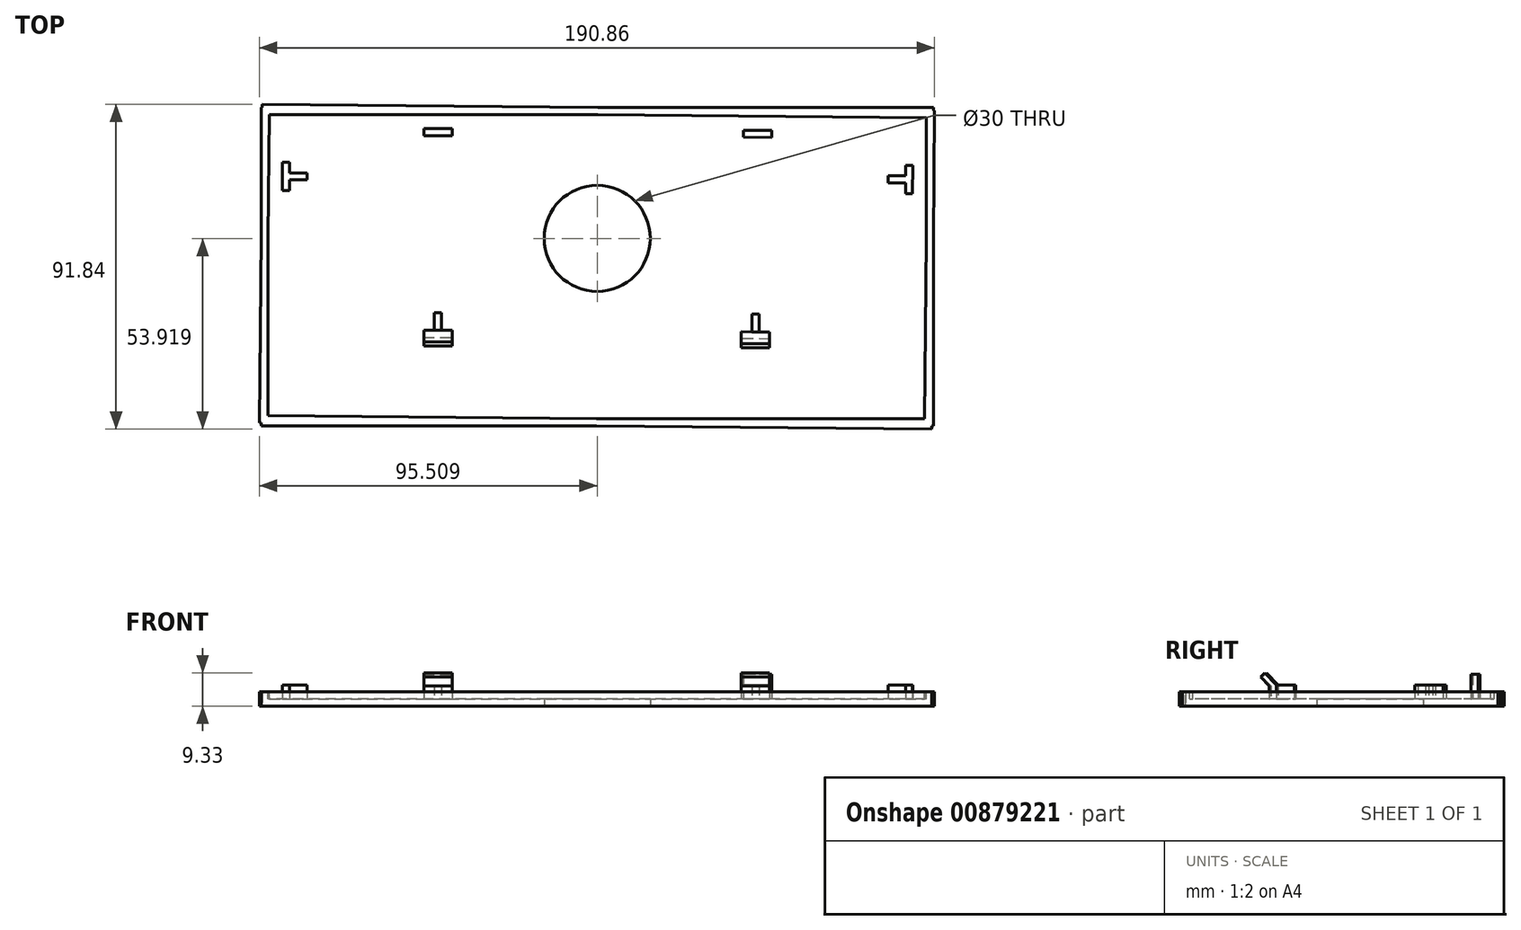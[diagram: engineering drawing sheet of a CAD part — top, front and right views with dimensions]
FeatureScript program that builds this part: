
annotation { "Feature Type Name" : "Feature", "Feature Type Description" : "" }
export const myFeature = defineFeature(function(context is Context, id is Id, definition is map)
    precondition{}
    {
        {
            var Q0;
            Q0=qCreatedBy(makeId("Top.planeOp"),FACE);
            var sketch = newSketch(context, id + "F0", { "sketchPlane" : qUnion([Q0])});
            skLineSegment(sketch, "E0.bottom", {"start": v(-112.44, 46.32) * mm, "end": v(77.56, 46.32) * mm});
            skLineSegment(sketch, "E0.top", {"start": v(-112.44, -43.68) * mm, "end": v(77.56, -43.68) * mm});
            skLineSegment(sketch, "E0.left", {"start": v(-112.44, 46.32) * mm, "end": v(-112.44, -43.68) * mm});
            skLineSegment(sketch, "E0.right", {"start": v(77.56, 46.32) * mm, "end": v(77.56, -43.68) * mm});
            skLineSegment(sketch, "E1.0", {"start": v(-110.44, 44.32) * mm, "end": v(-110.44, -41.68) * mm});
            skLineSegment(sketch, "E1.1", {"start": v(-110.44, 44.32) * mm, "end": v(75.56, 44.32) * mm});
            skLineSegment(sketch, "E1.2", {"start": v(75.56, 44.32) * mm, "end": v(75.56, -41.68) * mm});
            skLineSegment(sketch, "E1.3", {"start": v(-110.44, -41.68) * mm, "end": v(75.56, -41.68) * mm});
            skCircle(sketch, "E2", {"center": v(-17.44, 9.32) * mm, "radius": 15 * mm});
            skLineSegment(sketch, "E3.bottom", {"start": v(-106.44, 30.84) * mm, "end": v(-104.44, 30.84) * mm});
            skLineSegment(sketch, "E3.top", {"start": v(-106.44, 22.84) * mm, "end": v(-104.44, 22.84) * mm});
            skLineSegment(sketch, "E3.left", {"start": v(-106.44, 30.84) * mm, "end": v(-106.44, 22.84) * mm});
            skLineSegment(sketch, "E3.right", {"start": v(-104.44, 30.84) * mm, "end": v(-104.44, 22.84) * mm});
            skLineSegment(sketch, "E4", {"start": v(-17.23, 53.53) * mm, "end": v(-17.44, 9.32) * mm, "construction": true});
            skLineSegment(sketch, "E5", {"start": v(-17.44, 9.32) * mm, "end": v(-17.74, -52.58) * mm, "construction": true});
            skLineSegment(sketch, "E6.MirrorCS", {"start": v(71.76, 29.98) * mm, "end": v(71.69, 21.98) * mm});
            skLineSegment(sketch, "E7.MirrorCS", {"start": v(69.76, 30) * mm, "end": v(69.69, 22) * mm});
            skLineSegment(sketch, "E8.MirrorCS", {"start": v(71.69, 21.98) * mm, "end": v(69.69, 22) * mm});
            skLineSegment(sketch, "E9.MirrorCS", {"start": v(71.76, 29.98) * mm, "end": v(69.76, 30) * mm});
            skLineSegment(sketch, "E10.bottom", {"start": v(-66.44, 40.32) * mm, "end": v(-58.44, 40.32) * mm});
            skLineSegment(sketch, "E10.top", {"start": v(-66.44, 38.32) * mm, "end": v(-58.44, 38.32) * mm});
            skLineSegment(sketch, "E10.left", {"start": v(-66.44, 40.32) * mm, "end": v(-66.44, 38.32) * mm});
            skLineSegment(sketch, "E10.right", {"start": v(-58.44, 40.32) * mm, "end": v(-58.44, 38.32) * mm});
            skLineSegment(sketch, "E11.MirrorCS", {"start": v(31.86, 39.84) * mm, "end": v(23.86, 39.92) * mm});
            skLineSegment(sketch, "E12.MirrorCS", {"start": v(31.84, 37.84) * mm, "end": v(23.84, 37.92) * mm});
            skLineSegment(sketch, "E13.MirrorCS", {"start": v(23.86, 39.92) * mm, "end": v(23.84, 37.92) * mm});
            skLineSegment(sketch, "E14.MirrorCS", {"start": v(31.86, 39.84) * mm, "end": v(31.84, 37.84) * mm});
            skLineSegment(sketch, "E15.bottom", {"start": v(-66.44, -16.68) * mm, "end": v(-58.44, -16.68) * mm});
            skLineSegment(sketch, "E15.top", {"start": v(-66.44, -18.68) * mm, "end": v(-58.44, -18.68) * mm});
            skLineSegment(sketch, "E15.left", {"start": v(-66.44, -16.68) * mm, "end": v(-66.44, -18.68) * mm});
            skLineSegment(sketch, "E15.right", {"start": v(-58.44, -16.68) * mm, "end": v(-58.44, -18.68) * mm});
            skLineSegment(sketch, "E16.MirrorCS", {"start": v(31.3, -17.15) * mm, "end": v(23.3, -17.08) * mm});
            skLineSegment(sketch, "E17.MirrorCS", {"start": v(31.29, -19.15) * mm, "end": v(23.29, -19.08) * mm});
            skLineSegment(sketch, "E18.MirrorCS", {"start": v(23.3, -17.08) * mm, "end": v(23.29, -19.08) * mm});
            skLineSegment(sketch, "E19.MirrorCS", {"start": v(31.3, -17.15) * mm, "end": v(31.29, -19.15) * mm});
            skLineSegment(sketch, "E20.bottom", {"start": v(-104.44, 27.84) * mm, "end": v(-99.44, 27.84) * mm});
            skLineSegment(sketch, "E20.top", {"start": v(-104.44, 25.84) * mm, "end": v(-99.44, 25.84) * mm});
            skLineSegment(sketch, "E20.left", {"start": v(-104.44, 27.84) * mm, "end": v(-104.44, 25.84) * mm});
            skLineSegment(sketch, "E20.right", {"start": v(-99.44, 27.84) * mm, "end": v(-99.44, 25.84) * mm});
            skPoint(sketch, "E20.middle", {"position": v(-101.94, 26.84) * mm});
            skPoint(sketch, "E20.middle.positionSnap0", {"position": v(-104.44, 26.84) * mm});
            skPoint(sketch, "E20.centerSnap0", {"position": v(-104.44, 26.84) * mm});
            skPoint(sketch, "E21.MirrorP", {"position": v(67.22, 26.02) * mm});
            skLineSegment(sketch, "E22.MirrorCS", {"start": v(64.73, 27.05) * mm, "end": v(64.72, 25.05) * mm});
            skLineSegment(sketch, "E23.MirrorCS", {"start": v(69.72, 25) * mm, "end": v(64.72, 25.05) * mm});
            skLineSegment(sketch, "E24.MirrorCS", {"start": v(69.73, 27) * mm, "end": v(64.73, 27.05) * mm});
            skLineSegment(sketch, "E25.bottom", {"start": v(-63.44, -16.68) * mm, "end": v(-61.44, -16.68) * mm});
            skLineSegment(sketch, "E25.top", {"start": v(-63.44, -11.68) * mm, "end": v(-61.44, -11.68) * mm});
            skLineSegment(sketch, "E25.left", {"start": v(-63.44, -16.68) * mm, "end": v(-63.44, -11.68) * mm});
            skLineSegment(sketch, "E25.right", {"start": v(-61.44, -16.68) * mm, "end": v(-61.44, -11.68) * mm});
            skPoint(sketch, "E25.middle", {"position": v(-62.44, -14.18) * mm});
            skPoint(sketch, "E25.middle.positionSnap0", {"position": v(-62.44, -16.68) * mm});
            skPoint(sketch, "E25.centerSnap0", {"position": v(-62.44, -16.68) * mm});
            skLineSegment(sketch, "E26.MirrorCS", {"start": v(28.35, -12.13) * mm, "end": v(26.35, -12.1) * mm});
            skLineSegment(sketch, "E27.MirrorCS", {"start": v(28.3, -17.13) * mm, "end": v(28.35, -12.13) * mm});
            skLineSegment(sketch, "E28.MirrorCS", {"start": v(26.3, -17.1) * mm, "end": v(26.35, -12.1) * mm});
            skLineSegment(sketch, "E29.MirrorCS", {"start": v(28.3, -17.13) * mm, "end": v(26.3, -17.1) * mm});
            skSolve(sketch);
        }
        {
            var Q0;
            Q0=makeQuery(id+"F0.imprint","IMPRINT",FACE,{"disambiguationData":[TD([[makeQuery(id+"F0.imprint","IMPRINT",EDGE,{"derivedFrom":sQuery(id+"F0.wireOp",EDGE,"E0.bottom")}),-1.0]])]});
            extrude(context, id + "F1", {"entities" : qUnion([Q0]), "depth" : 4 * mm, "offsetDistance" : 25 * mm});
        }
        {
            var Q0;
            Q0=makeQuery(id+"F0.imprint","IMPRINT",FACE,{"disambiguationData":[TD([[makeQuery(id+"F0.imprint","IMPRINT",EDGE,{"derivedFrom":sQuery(id+"F0.wireOp",EDGE,"E1.0")}),1.0]])]});
            extrude(context, id + "F2", {"entities" : qUnion([Q0]), "operationType" : NewBodyOperationType.ADD, "depth" : 2 * mm, "offsetDistance" : 25 * mm});
        }
        {
            var Q0;
            Q0=makeQuery(id+"F0.imprint","IMPRINT",FACE,{"disambiguationData":[TD([[makeQuery(id+"F0.imprint","IMPRINT",EDGE,{"derivedFrom":sQuery(id+"F0.wireOp",EDGE,"E10.bottom")}),-1.0]])]});
            var Q1;
            Q1=makeQuery(id+"F0.imprint","IMPRINT",FACE,{"disambiguationData":[TD([[makeQuery(id+"F0.imprint","IMPRINT",EDGE,{"derivedFrom":sQuery(id+"F0.wireOp",EDGE,"E11.MirrorCS")}),1.0]])]});
            extrude(context, id + "F3", {"entities" : qUnion([Q0, Q1]), "operationType" : NewBodyOperationType.ADD, "depth" : 9 * mm, "offsetDistance" : 25 * mm});
        }
        {
            var Q0;
            {var subQ1=sQuery(id+"F0.wireOp",EDGE,"E3.bottom");Q0=makeQuery(id+"F0.imprint","IMPRINT",FACE,{"disambiguationData":[TD([[makeQuery(id+"F0.imprint","IMPRINT",EDGE,{"derivedFrom":subQ1}),-1.0]])]});}
            var Q1;
            Q1=makeQuery(id+"F0.imprint","IMPRINT",FACE,{"disambiguationData":[TD([[makeQuery(id+"F0.imprint","IMPRINT",EDGE,{"derivedFrom":sQuery(id+"F0.wireOp",EDGE,"E20.bottom")}),-1.0]])]});
            var Q2;
            Q2=makeQuery(id+"F0.imprint","IMPRINT",FACE,{"disambiguationData":[TD([[makeQuery(id+"F0.imprint","IMPRINT",EDGE,{"derivedFrom":sQuery(id+"F0.wireOp",EDGE,"E15.top")}),1.0]])]});
            var Q3;
            Q3=makeQuery(id+"F0.imprint","IMPRINT",FACE,{"disambiguationData":[TD([[makeQuery(id+"F0.imprint","IMPRINT",EDGE,{"derivedFrom":sQuery(id+"F0.wireOp",EDGE,"E25.bottom")}),1.0]])]});
            var Q4;
            Q4=makeQuery(id+"F0.imprint","IMPRINT",FACE,{"disambiguationData":[TD([[makeQuery(id+"F0.imprint","IMPRINT",EDGE,{"derivedFrom":sQuery(id+"F0.wireOp",EDGE,"E17.MirrorCS")}),-1.0]])]});
            var Q5;
            Q5=makeQuery(id+"F0.imprint","IMPRINT",FACE,{"disambiguationData":[TD([[makeQuery(id+"F0.imprint","IMPRINT",EDGE,{"derivedFrom":sQuery(id+"F0.wireOp",EDGE,"E26.MirrorCS")}),1.0]])]});
            var Q6;
            Q6=makeQuery(id+"F0.imprint","IMPRINT",FACE,{"disambiguationData":[TD([[makeQuery(id+"F0.imprint","IMPRINT",EDGE,{"derivedFrom":sQuery(id+"F0.wireOp",EDGE,"E6.MirrorCS")}),-1.0]])]});
            var Q7;
            Q7=makeQuery(id+"F0.imprint","IMPRINT",FACE,{"disambiguationData":[TD([[makeQuery(id+"F0.imprint","IMPRINT",EDGE,{"derivedFrom":sQuery(id+"F0.wireOp",EDGE,"E22.MirrorCS")}),1.0]])]});
            extrude(context, id + "F4", {"entities" : qUnion([Q0, Q1, Q2, Q3, Q4, Q5, Q6, Q7]), "operationType" : NewBodyOperationType.ADD, "depth" : 6 * mm, "offsetDistance" : 25 * mm});
        }
        {
            var Q0;
            {var subQ0=sQuery(id+"F0.wireOp",EDGE,"E15.bottom");Q0=makeQuery(id+"F4.opExtrude","CAP_EDGE",EDGE,{"disambiguationData":[OSD([subQ0]),TDD([makeQuery(id+"F0.imprint","IMPRINT",EDGE,{"disambiguationData":[TD([[makeQuery(id+"F0.imprint","INTERSECT",VERTEX,{"derivedFrom":[subQ0,sQuery(id+"F0.wireOp",EDGE,"E15.right")]}),1.0]])],"derivedFrom":subQ0})])],"isStart":false});}
            cPlane(context, id + "F5", {"entities" : qUnion([Q0]), "cplaneType" : CPlaneType.LINE_ANGLE, "offset" : 25 * mm, "angle" : 45 * degree, "width" : 150 * mm, "height" : 150 * mm});
        }
        {
            var Q0;
            Q0=qCreatedBy(id+"F5.planeOp",FACE);
            var sketch = newSketch(context, id + "F6", { "sketchPlane" : qUnion([Q0])});
            skLineSegment(sketch, "E30.0", {"start": v(61.44, 16.04) * mm, "end": v(58.44, 16.04) * mm});
            skLineSegment(sketch, "E31.0", {"start": v(66.44, 16.04) * mm, "end": v(63.44, 16.04) * mm});
            skLineSegment(sketch, "E32.bottom", {"start": v(58.44, 16.04) * mm, "end": v(66.44, 16.04) * mm});
            skLineSegment(sketch, "E32.top", {"start": v(58.44, 20.74) * mm, "end": v(66.44, 20.74) * mm});
            skLineSegment(sketch, "E32.left", {"start": v(58.44, 16.04) * mm, "end": v(58.44, 20.74) * mm});
            skLineSegment(sketch, "E32.right", {"start": v(66.44, 16.04) * mm, "end": v(66.44, 20.74) * mm});
            skSolve(sketch);
        }
        {
            var Q0;
            Q0=makeQuery(id+"F6.imprint","IMPRINT",FACE,{"disambiguationData":[TD([[makeQuery(id+"F6.imprint","IMPRINT",EDGE,{"derivedFrom":sQuery(id+"F6.wireOp",EDGE,"E32.top")}),-1.0]])]});
            extrude(context, id + "F7", {"entities" : qUnion([Q0]), "operationType" : NewBodyOperationType.ADD, "oppositeDirection" : true, "depth" : 1.6 * mm, "offsetDistance" : 25 * mm});
        }
        {
            var Q0;
            Q0=sQuery(id+"F0.wireOp",EDGE,"E5");
            cPlane(context, id + "F8", {"entities" : qUnion([Q0]), "cplaneType" : CPlaneType.LINE_ANGLE, "offset" : 25 * mm, "angle" : 90 * degree, "width" : 150 * mm, "height" : 150 * mm});
        }
        {
            var Q0;
            Q0=makeQuery(id+"F1.opExtrude","SWEPT_BODY",BODY,{"disambiguationData":[OSD([sQuery(id+"F0.wireOp",EDGE,"E0.bottom"),sQuery(id+"F0.wireOp",EDGE,"E0.top"),sQuery(id+"F0.wireOp",EDGE,"E0.left"),sQuery(id+"F0.wireOp",EDGE,"E0.right"),sQuery(id+"F0.wireOp",EDGE,"E1.0"),sQuery(id+"F0.wireOp",EDGE,"E1.1"),sQuery(id+"F0.wireOp",EDGE,"E1.2"),sQuery(id+"F0.wireOp",EDGE,"E1.3")])]});
            var Q1;
            Q1=qCreatedBy(id+"F8.planeOp",FACE);
            mirror(context, id + "F9", {"operationType" : NewBodyOperationType.ADD, "entities" : qUnion([Q0]), "mirrorPlane" : qUnion([Q1])});
        }
    });
